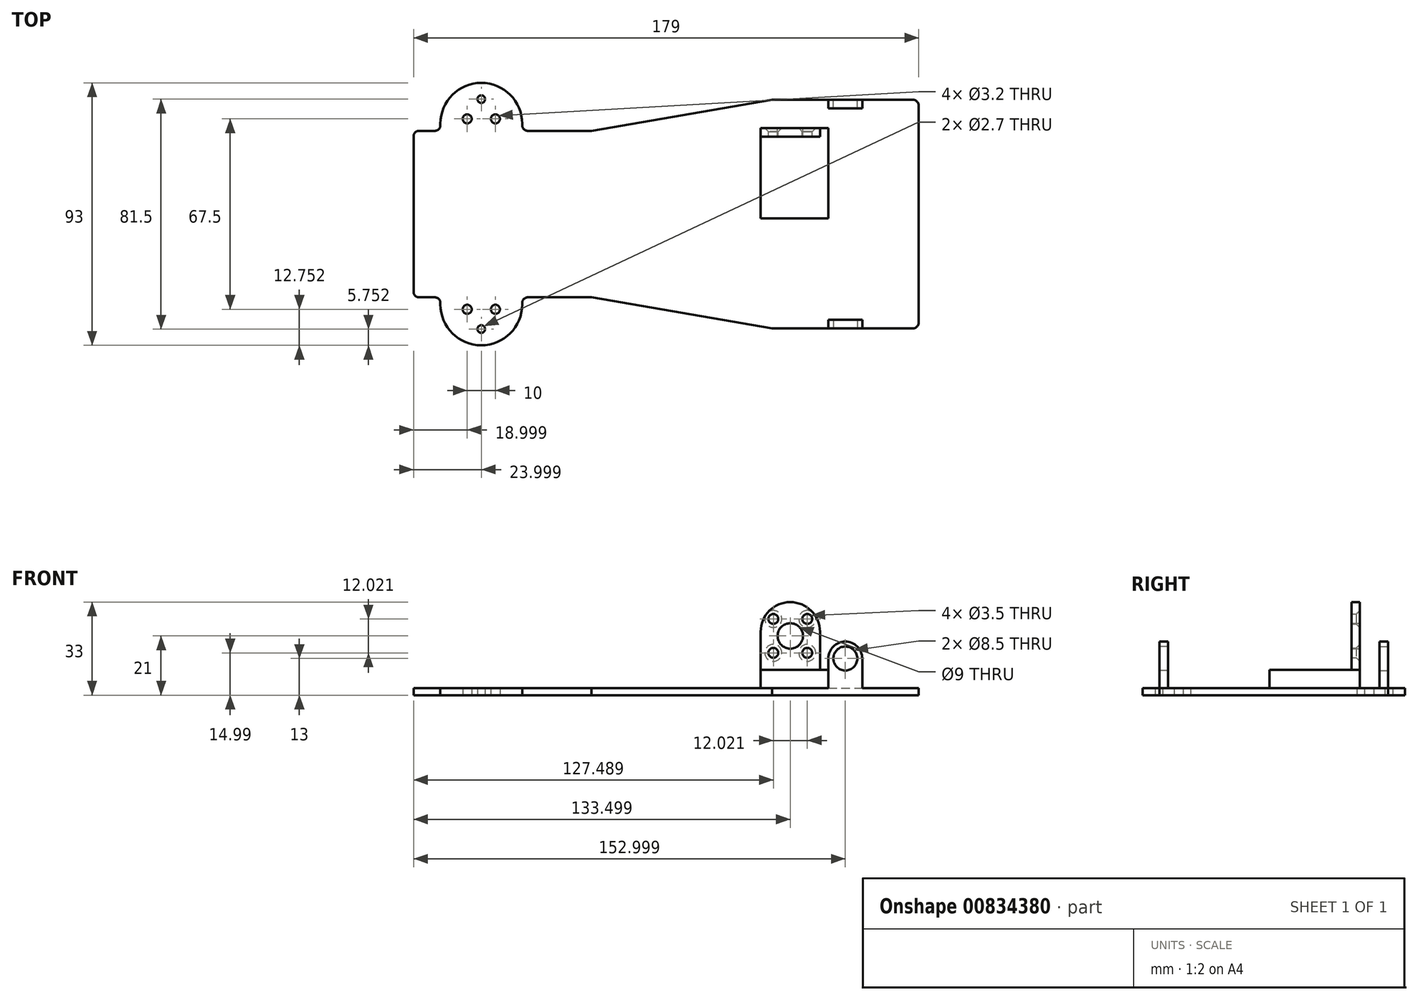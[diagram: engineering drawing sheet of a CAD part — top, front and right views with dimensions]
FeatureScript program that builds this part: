
annotation { "Feature Type Name" : "Feature", "Feature Type Description" : "" }
export const myFeature = defineFeature(function(context is Context, id is Id, definition is map)
    precondition{}
    {
        {
            var Q0;
            Q0=qCreatedBy(makeId("Top.planeOp"),FACE);
            var sketch = newSketch(context, id + "F0", { "sketchPlane" : qUnion([Q0])});
            skLineSegment(sketch, "E0", {"start": v(-202.4, -13.92) * mm, "end": v(73.01, -13.92) * mm});
            skLineSegment(sketch, "E1", {"start": v(-202.4, -13.92) * mm, "end": v(-202.4, 13.58) * mm});
            skLineSegment(sketch, "E2", {"start": v(-200.4, 15.58) * mm, "end": v(-194.9, 15.58) * mm});
            skLineSegment(sketch, "E3", {"start": v(-192.9, 17.58) * mm, "end": v(-192.9, 18.08) * mm});
            skLineSegment(sketch, "E4", {"start": v(-192.9, 18.08) * mm, "end": v(-163.9, 18.08) * mm});
            skLineSegment(sketch, "E5", {"start": v(-163.9, 18.08) * mm, "end": v(-163.9, 17.58) * mm});
            skLineSegment(sketch, "E6", {"start": v(-161.9, 15.58) * mm, "end": v(-139.4, 15.58) * mm});
            skLineSegment(sketch, "E7", {"start": v(-139.4, 15.58) * mm, "end": v(-139.4, -13.92) * mm});
            skArc(sketch, "E8", {"start": v(-163.9, 18.08) * mm, "mid": v(-178.4, 32.58) * mm, "end": v(-192.9, 18.08) * mm});
            skLineSegment(sketch, "E9", {"start": v(-75.4, -13.92) * mm, "end": v(-75.4, 26.58) * mm});
            skLineSegment(sketch, "E10", {"start": v(-75.4, 26.58) * mm, "end": v(-25.4, 26.58) * mm});
            skLineSegment(sketch, "E11", {"start": v(-23.4, 24.58) * mm, "end": v(-23.4, -13.92) * mm});
            skLineSegment(sketch, "E12", {"start": v(-139.4, 15.58) * mm, "end": v(-75.4, 26.58) * mm});
            skLineSegment(sketch, "E13.MirrorCS", {"start": v(-202.4, -13.92) * mm, "end": v(-202.4, -41.42) * mm});
            skLineSegment(sketch, "E14.MirrorCS", {"start": v(-200.4, -43.42) * mm, "end": v(-194.9, -43.42) * mm});
            skLineSegment(sketch, "E15.MirrorCS", {"start": v(-192.9, -45.42) * mm, "end": v(-192.9, -45.92) * mm});
            skArc(sketch, "E16.MirrorCS", {"start": v(-163.9, -45.92) * mm, "mid": v(-178.4, -60.42) * mm, "end": v(-192.9, -45.92) * mm});
            skLineSegment(sketch, "E17.MirrorCS", {"start": v(-163.9, -45.92) * mm, "end": v(-163.9, -45.42) * mm});
            skLineSegment(sketch, "E18.MirrorCS", {"start": v(-161.9, -43.42) * mm, "end": v(-139.4, -43.42) * mm});
            skLineSegment(sketch, "E19.MirrorCS", {"start": v(-139.4, -43.42) * mm, "end": v(-75.4, -54.42) * mm});
            skLineSegment(sketch, "E20.MirrorCS", {"start": v(-75.4, -54.42) * mm, "end": v(-25.4, -54.42) * mm});
            skLineSegment(sketch, "E21.MirrorCS", {"start": v(-23.4, -52.42) * mm, "end": v(-23.4, -13.92) * mm});
            skPoint(sketch, "E22.visualSharp", {"position": v(-192.9, 15.58) * mm});
            skArc(sketch, "E22.filletArc", {"start": v(-194.9, 15.58) * mm, "mid": v(-193.48, 16.17) * mm, "end": v(-192.9, 17.58) * mm});
            skPoint(sketch, "E23.visualSharp", {"position": v(-163.9, 15.58) * mm});
            skArc(sketch, "E23.filletArc", {"start": v(-163.9, 17.58) * mm, "mid": v(-163.3, 16.17) * mm, "end": v(-161.9, 15.58) * mm});
            skPoint(sketch, "E24.visualSharp", {"position": v(-192.9, -43.42) * mm});
            skArc(sketch, "E24.filletArc", {"start": v(-192.9, -45.42) * mm, "mid": v(-193.48, -44) * mm, "end": v(-194.9, -43.42) * mm});
            skPoint(sketch, "E25.visualSharp", {"position": v(-163.9, -43.42) * mm});
            skArc(sketch, "E25.filletArc", {"start": v(-161.9, -43.42) * mm, "mid": v(-163.3, -44) * mm, "end": v(-163.9, -45.42) * mm});
            skPoint(sketch, "E26.visualSharp", {"position": v(-202.4, 15.58) * mm});
            skArc(sketch, "E26.filletArc", {"start": v(-200.4, 15.58) * mm, "mid": v(-201.8, 15) * mm, "end": v(-202.4, 13.58) * mm});
            skPoint(sketch, "E27.visualSharp", {"position": v(-202.4, -43.42) * mm});
            skArc(sketch, "E27.filletArc", {"start": v(-202.4, -41.42) * mm, "mid": v(-201.8, -42.83) * mm, "end": v(-200.4, -43.42) * mm});
            skPoint(sketch, "E28.visualSharp", {"position": v(-23.4, -54.42) * mm});
            skArc(sketch, "E28.filletArc", {"start": v(-25.4, -54.42) * mm, "mid": v(-23.98, -53.83) * mm, "end": v(-23.4, -52.42) * mm});
            skPoint(sketch, "E29.visualSharp", {"position": v(-23.4, 26.58) * mm});
            skArc(sketch, "E29.filletArc", {"start": v(-23.4, 24.58) * mm, "mid": v(-23.98, 26) * mm, "end": v(-25.4, 26.58) * mm});
            skLineSegment(sketch, "E30", {"start": v(-178.4, -68.7) * mm, "end": v(-178.4, 42.47) * mm});
            skCircle(sketch, "E31", {"center": v(-183.4, -47.67) * mm, "radius": 1.6 * mm});
            skCircle(sketch, "E32", {"center": v(-178.4, -54.67) * mm, "radius": 1.35 * mm});
            skCircle(sketch, "E33.MirrorC", {"center": v(-173.4, -47.67) * mm, "radius": 1.6 * mm});
            skCircle(sketch, "E34.MirrorC", {"center": v(-183.4, 19.83) * mm, "radius": 1.6 * mm});
            skCircle(sketch, "E35.MirrorC", {"center": v(-173.4, 19.83) * mm, "radius": 1.6 * mm});
            skCircle(sketch, "E36.MirrorC", {"center": v(-178.4, 26.83) * mm, "radius": 1.35 * mm});
            skLineSegment(sketch, "E37", {"start": v(-43.4, -54.42) * mm, "end": v(-43.4, 26.58) * mm});
            skLineSegment(sketch, "E38", {"start": v(-63.4, -54.42) * mm, "end": v(-63.4, 26.58) * mm});
            skSolve(sketch);
        }
        {
            var Q0;
            Q0 = qSketchRegion(id + "F0", true);
            extrude(context, id + "F1", {"entities" : qUnion([Q0]), "depth" : 2.5 * mm, "offsetDistance" : 25 * mm});
        }
        {
            var Q0;
            Q0=qCreatedBy(makeId("Top.planeOp"),FACE);
            var sketch = newSketch(context, id + "F2", { "sketchPlane" : qUnion([Q0])});
            skLineSegment(sketch, "E39.bottom", {"start": v(-43.4, -54.42) * mm, "end": v(-43.4, 26.58) * mm});
            skLineSegment(sketch, "E39.top", {"start": v(-55.4, -54.42) * mm, "end": v(-55.4, -15.42) * mm});
            skLineSegment(sketch, "E39.left", {"start": v(-43.4, -54.42) * mm, "end": v(-55.4, -54.42) * mm});
            skLineSegment(sketch, "E39.right", {"start": v(-43.4, 26.58) * mm, "end": v(-55.4, 26.58) * mm});
            skLineSegment(sketch, "E40", {"start": v(-55.4, -15.42) * mm, "end": v(-79.4, -15.42) * mm});
            skLineSegment(sketch, "E41", {"start": v(-79.4, -15.42) * mm, "end": v(-79.4, 16.58) * mm});
            skLineSegment(sketch, "E42", {"start": v(-79.4, 16.58) * mm, "end": v(-55.4, 16.58) * mm});
            skLineSegment(sketch, "E43.trimOffspring", {"start": v(-55.4, 16.58) * mm, "end": v(-55.4, 26.58) * mm});
            skPoint(sketch, "E44.centerSnap0", {"position": v(-49.4, -54.42) * mm});
            skPoint(sketch, "E45", {"position": v(-55.4, -54.42) * mm});
            skPoint(sketch, "E46", {"position": v(-43.4, -54.42) * mm});
            skPoint(sketch, "E47", {"position": v(-79.4, 16.58) * mm});
            skPoint(sketch, "E48", {"position": v(-43.4, 26.58) * mm});
            skPoint(sketch, "E49", {"position": v(-55.4, 26.58) * mm});
            skSolve(sketch);
        }
        {
            var Q0;
            Q0=qCreatedBy(makeId("Front.planeOp"),FACE);
            var Q1;
            Q1=sQuery(id+"F0.wireOp",VERTEX,"E28.visualSharp");
            cPlane(context, id + "F3", {"entities" : qUnion([Q0, Q1]), "cplaneType" : CPlaneType.PLANE_POINT, "offset" : 25 * mm, "width" : 150 * mm, "height" : 150 * mm});
        }
        {
            var Q0;
            Q0=qCreatedBy(makeId("Front.planeOp"),FACE);
            var Q1;
            Q1=sQuery(id+"F2.wireOp",VERTEX,"E39.right.end");
            cPlane(context, id + "F4", {"entities" : qUnion([Q0, Q1]), "cplaneType" : CPlaneType.PLANE_POINT, "offset" : 25 * mm, "width" : 150 * mm, "height" : 150 * mm});
        }
        {
            var Q0;
            Q0=qCreatedBy(makeId("Front.planeOp"),FACE);
            var Q1;
            Q1=sQuery(id+"F2.wireOp",VERTEX,"E42.end");
            cPlane(context, id + "F5", {"entities" : qUnion([Q0, Q1]), "cplaneType" : CPlaneType.PLANE_POINT, "offset" : 25 * mm, "width" : 150 * mm, "height" : 150 * mm});
        }
        {
            var Q0;
            Q0=qCreatedBy(id+"F3.planeOp",FACE);
            var sketch = newSketch(context, id + "F6", { "sketchPlane" : qUnion([Q0])});
            skLineSegment(sketch, "E50.bottom", {"start": v(-55.4, 0) * mm, "end": v(-43.4, 0) * mm});
            skLineSegment(sketch, "E50.top", {"start": v(-55.4, 13) * mm, "end": v(-43.4, 13) * mm});
            skLineSegment(sketch, "E50.left", {"start": v(-55.4, 0) * mm, "end": v(-55.4, 13) * mm});
            skLineSegment(sketch, "E50.right", {"start": v(-43.4, 0) * mm, "end": v(-43.4, 13) * mm});
            skArc(sketch, "E51", {"start": v(-43.4, 13) * mm, "mid": v(-49.4, 19) * mm, "end": v(-55.4, 13) * mm});
            skCircle(sketch, "E52", {"center": v(-49.4, 13) * mm, "radius": 4.25 * mm});
            skSolve(sketch);
        }
        {
            var Q0;
            Q0 = qSketchRegion(id + "F6", true);
            extrude(context, id + "F7", {"entities" : qUnion([Q0]), "operationType" : NewBodyOperationType.ADD, "oppositeDirection" : true, "depth" : 3 * mm, "offsetDistance" : 25 * mm});
        }
        {
            var Q0;
            Q0=qCreatedBy(id+"F4.planeOp",FACE);
            var sketch = newSketch(context, id + "F8", { "sketchPlane" : qUnion([Q0])});
            skLineSegment(sketch, "E53.bottom", {"start": v(-55.4, 0) * mm, "end": v(-43.4, 0) * mm});
            skLineSegment(sketch, "E53.top", {"start": v(-55.4, 13) * mm, "end": v(-43.4, 13) * mm});
            skLineSegment(sketch, "E53.left", {"start": v(-55.4, 0) * mm, "end": v(-55.4, 13) * mm});
            skLineSegment(sketch, "E53.right", {"start": v(-43.4, 0) * mm, "end": v(-43.4, 13) * mm});
            skArc(sketch, "E54", {"start": v(-43.4, 13) * mm, "mid": v(-49.4, 19) * mm, "end": v(-55.4, 13) * mm});
            skCircle(sketch, "E55", {"center": v(-49.4, 13) * mm, "radius": 4.25 * mm});
            skSolve(sketch);
        }
        {
            var Q0;
            Q0 = qSketchRegion(id + "F8", true);
            extrude(context, id + "F9", {"entities" : qUnion([Q0]), "operationType" : NewBodyOperationType.ADD, "depth" : 3 * mm, "offsetDistance" : 25 * mm});
        }
        {
            var Q0;
            Q0=qCreatedBy(id+"F5.planeOp",FACE);
            var sketch = newSketch(context, id + "F10", { "sketchPlane" : qUnion([Q0])});
            skLineSegment(sketch, "E56.bottom", {"start": v(-79.4, 0) * mm, "end": v(-58.4, 0) * mm});
            skLineSegment(sketch, "E56.top", {"start": v(-79.4, 22.5) * mm, "end": v(-58.4, 22.5) * mm});
            skLineSegment(sketch, "E56.left", {"start": v(-79.4, 0) * mm, "end": v(-79.4, 22.5) * mm});
            skLineSegment(sketch, "E56.right", {"start": v(-58.4, 0) * mm, "end": v(-58.4, 22.5) * mm});
            skArc(sketch, "E57", {"start": v(-58.4, 22.5) * mm, "mid": v(-68.9, 33) * mm, "end": v(-79.4, 22.5) * mm});
            skCircle(sketch, "E58", {"center": v(-68.9, 21) * mm, "radius": 4.5 * mm});
            skPoint(sketch, "E58.centerSnap0", {"position": v(-68.9, 33) * mm});
            skLineSegment(sketch, "E59", {"start": v(-74.9, 27.01) * mm, "end": v(-68.9, 21) * mm});
            skLineSegment(sketch, "E60", {"start": v(-68.9, 33) * mm, "end": v(-68.9, 13.34) * mm});
            skLineSegment(sketch, "E61", {"start": v(-68.9, 21) * mm, "end": v(-77.03, 21) * mm});
            skPoint(sketch, "E62", {"position": v(-74.9, 27.01) * mm});
            skPoint(sketch, "E63", {"position": v(-79.4, 0) * mm});
            skPoint(sketch, "E64.MirrorP", {"position": v(-74.9, 14.99) * mm});
            skPoint(sketch, "E65.MirrorP", {"position": v(-62.88, 27.01) * mm});
            skPoint(sketch, "E66.MirrorP", {"position": v(-62.88, 14.99) * mm});
            skSolve(sketch);
        }
        {
            var Q0;
            Q0 = qSketchRegion(id + "F10", true);
            extrude(context, id + "F11", {"entities" : qUnion([Q0]), "operationType" : NewBodyOperationType.ADD, "depth" : 3 * mm, "offsetDistance" : 25 * mm});
        }
        {
            var Q0;
            Q0=sQuery(id+"F10.wireOp",VERTEX,"E62");
            var Q1;
            Q1=sQuery(id+"F10.wireOp",VERTEX,"E65.MirrorP");
            var Q2;
            Q2=sQuery(id+"F10.wireOp",VERTEX,"E66.MirrorP");
            var Q3;
            Q3=sQuery(id+"F10.wireOp",VERTEX,"E64.MirrorP");
            var Q4;
            Q4=makeQuery(id+"F1.opExtrude","SWEPT_BODY",BODY,{"disambiguationData":[OSD([sQuery(id+"F0.wireOp",EDGE,"E1"),sQuery(id+"F0.wireOp",EDGE,"E2"),sQuery(id+"F0.wireOp",EDGE,"E3"),sQuery(id+"F0.wireOp",EDGE,"E5"),sQuery(id+"F0.wireOp",EDGE,"E6"),sQuery(id+"F0.wireOp",EDGE,"E8"),sQuery(id+"F0.wireOp",EDGE,"E10"),sQuery(id+"F0.wireOp",EDGE,"E11"),sQuery(id+"F0.wireOp",EDGE,"E12"),sQuery(id+"F0.wireOp",EDGE,"E13.MirrorCS"),sQuery(id+"F0.wireOp",EDGE,"E14.MirrorCS"),sQuery(id+"F0.wireOp",EDGE,"E15.MirrorCS"),sQuery(id+"F0.wireOp",EDGE,"E16.MirrorCS"),sQuery(id+"F0.wireOp",EDGE,"E17.MirrorCS"),sQuery(id+"F0.wireOp",EDGE,"E18.MirrorCS"),sQuery(id+"F0.wireOp",EDGE,"E19.MirrorCS"),sQuery(id+"F0.wireOp",EDGE,"E20.MirrorCS"),sQuery(id+"F0.wireOp",EDGE,"E21.MirrorCS"),sQuery(id+"F0.wireOp",EDGE,"E22.filletArc"),sQuery(id+"F0.wireOp",EDGE,"E23.filletArc"),sQuery(id+"F0.wireOp",EDGE,"E24.filletArc"),sQuery(id+"F0.wireOp",EDGE,"E25.filletArc"),sQuery(id+"F0.wireOp",EDGE,"E26.filletArc"),sQuery(id+"F0.wireOp",EDGE,"E27.filletArc"),sQuery(id+"F0.wireOp",EDGE,"E28.filletArc"),sQuery(id+"F0.wireOp",EDGE,"E29.filletArc"),sQuery(id+"F0.wireOp",EDGE,"E31"),sQuery(id+"F0.wireOp",EDGE,"E32"),sQuery(id+"F0.wireOp",EDGE,"E33.MirrorC"),sQuery(id+"F0.wireOp",EDGE,"E34.MirrorC"),sQuery(id+"F0.wireOp",EDGE,"E35.MirrorC"),sQuery(id+"F0.wireOp",EDGE,"E36.MirrorC")])]});
            hole(context, id + "F12", {"style" : HoleStyle.C_SINK, "endStyle" : HoleEndStyle.THROUGH, "oppositeDirection" : true, "holeDiameter" : 3.5 * mm, "cSinkDiameter" : 6 * mm, "cSinkAngle" : 90 * degree, "majorDiameter" : 5 * mm, "isTappedThrough" : true, "tappedDepth" : 12 * mm, "tapClearance" : 3, "startFromSketch" : true, "locations" : qUnion([Q0, Q1, Q2, Q3]), "scope" : qUnion([Q4])});
        }
        {
            var Q0;
            Q0=qCreatedBy(makeId("Front.planeOp"),FACE);
            var Q1;
            Q1=sQuery(id+"F2.wireOp",VERTEX,"E40.end");
            cPlane(context, id + "F13", {"entities" : qUnion([Q0, Q1]), "cplaneType" : CPlaneType.PLANE_POINT, "offset" : 25 * mm, "width" : 150 * mm, "height" : 150 * mm});
        }
        {
            var Q0;
            Q0=qCreatedBy(id+"F13.planeOp",FACE);
            var sketch = newSketch(context, id + "F14", { "sketchPlane" : qUnion([Q0])});
            skLineSegment(sketch, "E67.bottom", {"start": v(-79.4, 0) * mm, "end": v(-55.4, 0) * mm});
            skLineSegment(sketch, "E67.top", {"start": v(-79.4, 9) * mm, "end": v(-55.4, 9) * mm});
            skLineSegment(sketch, "E67.left", {"start": v(-79.4, 0) * mm, "end": v(-79.4, 9) * mm});
            skLineSegment(sketch, "E67.right", {"start": v(-55.4, 0) * mm, "end": v(-55.4, 9) * mm});
            skSolve(sketch);
        }
        {
            var Q0;
            Q0 = qSketchRegion(id + "F14", true);
            extrude(context, id + "F15", {"entities" : qUnion([Q0]), "operationType" : NewBodyOperationType.ADD, "oppositeDirection" : true, "depth" : 32 * mm, "offsetDistance" : 25 * mm});
        }
    });
